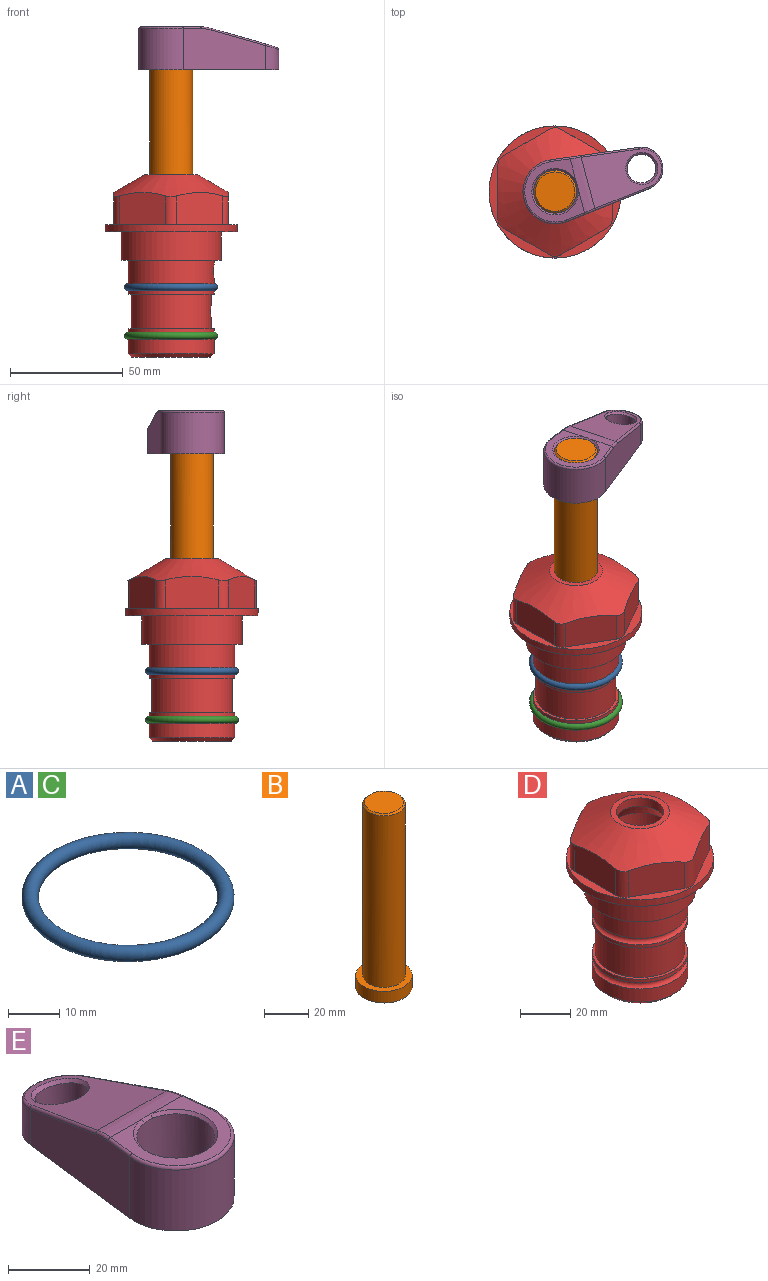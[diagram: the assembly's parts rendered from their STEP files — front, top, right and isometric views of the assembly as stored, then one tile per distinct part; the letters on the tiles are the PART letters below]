
ASSEMBLY  parts=5 mates=4
PART A: 1 faces, bbox 44.7x44.7x3.2 mm
  f0: torus R=19.05mm, axis (0,0,1), area 1193.9mm2
PART B: 6 faces, bbox 25.4x25.4x101.6 mm
  f0: plane 17.46x17.46mm, normal (0,0,1), area 239.5mm2, adj f5
  f1: plane 25.4x25.4mm, normal (0,0,-1), area 506.7mm2, adj f2
  f2: cylinder r=12.7mm len=25.4mm, axis (0,0,1), area 506.7mm2, adj f1,f3
  f3: plane 25.4x25.4mm, normal (0,0,1), area 221.7mm2, adj f2,f4
  f4: cylinder r=9.53mm len=94.46mm, axis (0,0,1), area 5653mm2, adj f3,f5
  f5: cone r=8.73mm half-angle=45deg, axis (0,0,-1), area 64.4mm2, adj f0,f4
PART C: same geometry as A
PART D: 36 faces, bbox 58.7x58.7x81 mm
  f0: cylinder r=17.78mm len=35.56mm, axis (0,0,1), area 1670.8mm2, adj f23,f24,f31
  f1: cylinder r=19.05mm len=38.1mm, axis (0,0,1), area 1191.9mm2, adj f26,f27,f30
  f2: plane 58.66x58.66mm, normal (0,0,-1), area 1150.6mm2, adj f3,f28
  f3: cylinder r=29.33mm len=58.66mm, axis (0,0,-1), area 585.1mm2, adj f2,f4
  f4: plane 58.66x58.66mm, normal (0,0,1), area 475.9mm2, adj f3,f5,f6,f7,f8,f9,f10,f11
  f5: plane 20.32x14.34mm, normal (-0.5,0.87,0), area 324.4mm2, adj f4,f15,f16,f17
  f6: plane 20.32x14.34mm, normal (0.5,0.87,0), area 324.4mm2, adj f4,f14,f15,f17
  f7: plane 23.48x14.34mm, normal (1,0,0), area 324.4mm2, adj f4,f13,f14,f17
  f8: plane 20.32x14.34mm, normal (0.5,-0.87,0), area 324.4mm2, adj f4,f12,f13,f17
  f9: plane 20.32x14.34mm, normal (-0.5,-0.87,0), area 324.4mm2, adj f4,f11,f12,f17
  f10: plane 23.48x14.34mm, normal (-1,0,0), area 324.4mm2, adj f4,f11,f16,f17
  f11: cylinder r=5.08mm len=12.85mm, axis (0,0,-1), area 67.2mm2, adj f4,f9,f10,f17
  f12: cylinder r=5.08mm len=12.85mm, axis (0,0,-1), area 67.2mm2, adj f4,f8,f9,f17
  f13: cylinder r=5.08mm len=12.85mm, axis (0,0,-1), area 67.2mm2, adj f4,f7,f8,f17
  f14: cylinder r=5.08mm len=12.85mm, axis (0,0,-1), area 67.2mm2, adj f4,f6,f7,f17
  f15: cylinder r=5.08mm len=12.85mm, axis (0,0,-1), area 67.2mm2, adj f4,f5,f6,f17
  f16: cylinder r=5.08mm len=12.85mm, axis (0,0,-1), area 67.2mm2, adj f4,f5,f10,f17
  f17: cone r=11.73mm half-angle=60deg, axis (0,0,-1), area 2071.8mm2, adj f5,f6,f7,f8,f9,f10,f11,f12
  f18: plane 23.46x23.46mm, normal (0,0,1), area 147.4mm2, adj f17,f35
  f19: plane 34.93x34.93mm, normal (0,0,-1), area 958mm2, adj f29
  f20: cylinder r=19.05mm len=38.1mm, axis (0,0,1), area 760.1mm2, adj f21,f29
  f21: torus R=19.05mm, axis (0,0,1), area 565.3mm2, adj f20,f22
  f22: cylinder r=19.05mm len=38.1mm, axis (0,0,1), area 190mm2, adj f21,f23
  f23: plane 38.1x38.1mm, normal (0,0,1), area 146.9mm2, adj f0,f22
  f24: plane 38.1x38.1mm, normal (0,0,-1), area 146.9mm2, adj f0,f25
  f25: cylinder r=19.05mm len=38.1mm, axis (0,0,1), area 190mm2, adj f24,f26
  f26: torus R=19.05mm, axis (0,0,1), area 565.3mm2, adj f1,f25
  f27: plane 44.45x44.45mm, normal (0,0,-1), area 411.7mm2, adj f1,f28
  f28: cylinder r=22.23mm len=44.45mm, axis (0,0,1), area 1773.5mm2, adj f2,f27
  f29: cone r=19.05mm half-angle=45deg, axis (0,0,1), area 257.5mm2, adj f19,f20
  f30: cylinder r=3.17mm len=6.75mm, axis (-1,0,0), area 128mm2, adj f1,f33
  f31: cylinder r=3.17mm len=6.35mm, axis (-1,0,0), area 102.5mm2, adj f0,f33
  f32: plane 25.4x25.4mm, normal (0,0,1), area 506.7mm2, adj f33
  f33: cylinder r=12.7mm len=66.42mm, axis (0,0,-1), area 5236.2mm2, adj f30,f31,f32,f34
  f34: cone r=9.53mm half-angle=30deg, axis (0,0,-1), area 443.4mm2, adj f33,f35
  f35: cylinder r=9.53mm len=19.05mm, axis (0,0,-1), area 240.9mm2, adj f18,f34
PART E: 31 faces, bbox 31.7x65.5x19.8 mm
  f0: plane 39.12x18.26mm, normal (0.99,0.12,0), area 612.2mm2, adj f1,f4,f7,f11,f13,f15
  f1: cylinder r=9.53mm len=18.91mm, axis (0,0,-1), area 296.1mm2, adj f0,f2,f7,f17
  f2: plane 39.12x18.26mm, normal (-0.99,0.12,0), area 612.2mm2, adj f1,f4,f7,f12,f14,f16
  f3: cylinder r=6.35mm len=12.7mm, axis (0,0,-1), area 362.4mm2, adj f7,f18
  f4: cylinder r=14.29mm len=28.58mm, axis (0,0,-1), area 882.2mm2, adj f0,f2,f7,f10
  f5: cylinder r=9.53mm len=19.05mm, axis (0,0,-1), area 1092.6mm2, adj f7,f19,f20
  f6: plane 26.99x23.69mm, normal (0,0,1), area 216.2mm2, adj f9,f10,f11,f12,f19
  f7: plane 63.5x28.58mm, normal (0,0,-1), area 661.8mm2, adj f0,f1,f2,f3,f4,f5,f22,f23
  f8: plane 33.52x23.6mm, normal (0,0.26,0.97), area 486mm2, adj f9,f15,f16,f17,f18
  f9: cylinder r=19.05mm len=24.72mm, axis (1,0,0), area 120.4mm2, adj f6,f8,f13,f14,f20
  f10: torus R=13.49mm, axis (0,0,1), area 59mm2, adj f4,f6,f11,f12
  f11: cylinder r=0.79mm len=8.67mm, axis (0.12,-0.99,0), area 10.8mm2, adj f0,f6,f10,f13
  f12: cylinder r=0.79mm len=8.67mm, axis (0.12,0.99,0), area 10.8mm2, adj f2,f6,f10,f14
  f13: bspline ~4.95x1.42mm, area 6.1mm2, adj f0,f9,f11,f15
  f14: bspline ~4.95x1.42mm, area 6.1mm2, adj f2,f9,f12,f16
  f15: cylinder r=0.79mm len=25.95mm, axis (0.12,-0.96,0.26), area 32.9mm2, adj f0,f8,f13,f17
  f16: cylinder r=0.79mm len=25.95mm, axis (0.12,0.96,-0.26), area 32.9mm2, adj f2,f8,f14,f17
  f17: bspline ~18.91x8.38mm, area 30mm2, adj f1,f8,f15,f16
  f18: bspline ~14.29x14.29mm, area 48.3mm2, adj f3,f8
  f19: cone r=9.53mm half-angle=45deg, axis (0,0,1), area 66.5mm2, adj f5,f6,f20
  f20: bspline ~3.22x0.96mm, area 3.5mm2, adj f5,f9,f19
  f21: plane 2.75x2.72mm, normal (0,0,-1), area 2.9mm2, adj f23,f25,f28
  f22: plane 23.05x15.88mm, normal (-0.99,-0.12,0), area 323.6mm2, adj f7,f25,f26,f27,f28,f29
  f23: plane 23.05x15.88mm, normal (0.99,-0.12,0), area 323.6mm2, adj f7,f21,f25,f27,f28,f30
  f24: cylinder r=9.53mm len=10.69mm, axis (0,0,-1), area 114.7mm2, adj f7,f27,f29,f30
  f25: cylinder r=12.7mm len=20.59mm, axis (0,0,-1), area 381.1mm2, adj f7,f21,f22,f23,f26,f28
  f26: plane 2.75x2.72mm, normal (0,0,-1), area 2.9mm2, adj f22,f25,f28
  f27: plane 19.72x18.37mm, normal (0,-0.26,-0.97), area 291.8mm2, adj f22,f23,f24,f28,f29,f30
  f28: cylinder r=15.88mm len=19.92mm, axis (1,0,0), area 54.8mm2, adj f21,f22,f23,f25,f26,f27
  f29: cylinder r=1.59mm len=11mm, axis (0,0,-1), area 34.7mm2, adj f7,f22,f24,f27
  f30: cylinder r=1.59mm len=11mm, axis (0,0,-1), area 34.7mm2, adj f7,f23,f24,f27
PLACE A at identity
PLACE B rot(axis=(0,0,-1),75.1deg) t=(0,0,27.55)mm
PLACE C t=(0,0,-21.59)mm
PLACE D at identity fixed
PLACE E rot(axis=(0,0,-1),75.1deg) t=(0,0,27.55)mm
MATE fastened A.f0 <-> D.f0  axis (0,0,1) through (0,0,-24.51)mm
MATE cylindrical B.f2 <-> D.f0  axis (0,0,-1) through (0,0,-10.55)mm
MATE fastened C.f0 <-> D.f0  axis (0,0,1) through (0,0,-46.1)mm
MATE fastened E.f4 <-> B.f2  axis (0,0,1) through (0,0,91.05)mm
